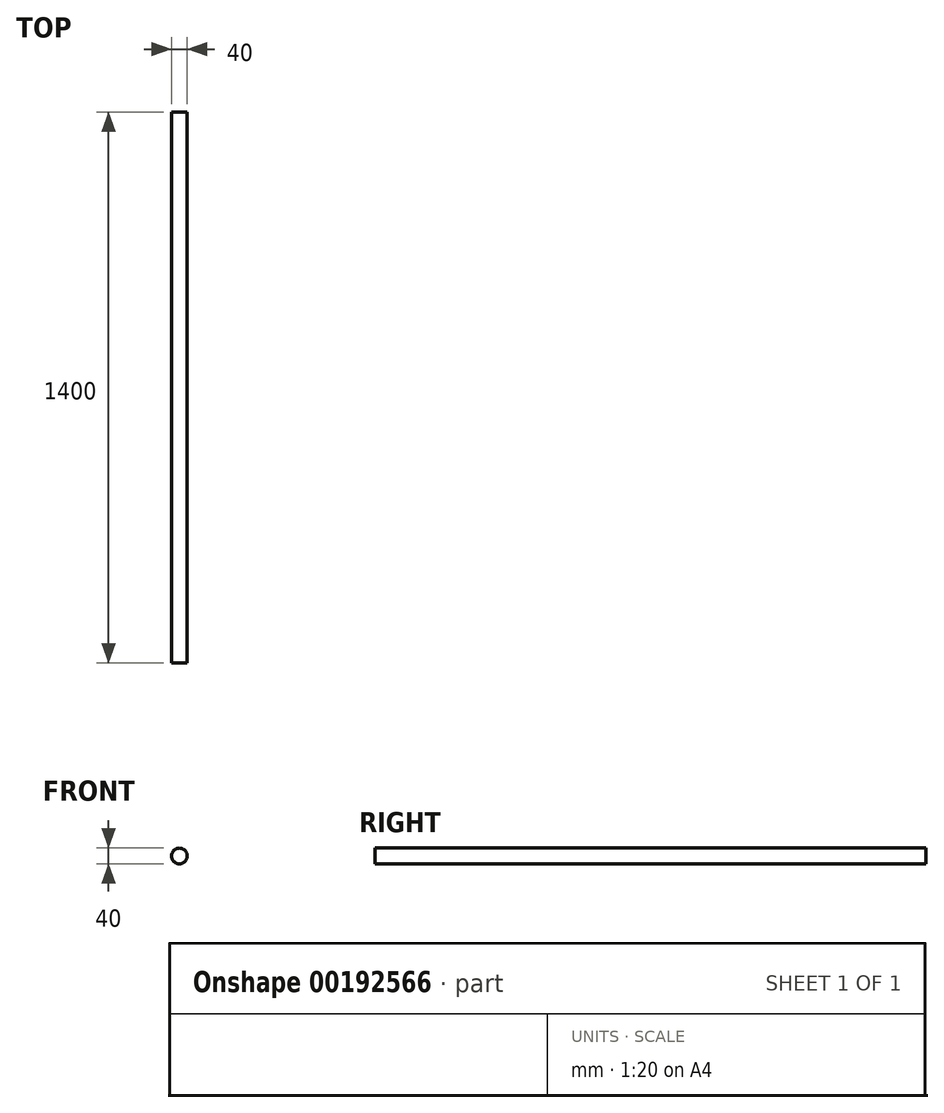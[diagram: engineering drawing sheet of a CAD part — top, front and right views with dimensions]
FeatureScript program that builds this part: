
annotation { "Feature Type Name" : "Feature", "Feature Type Description" : "" }
export const myFeature = defineFeature(function(context is Context, id is Id, definition is map)
    precondition{}
    {
        {
            var Q0;
            Q0=qCreatedBy(makeId("Front.planeOp"),FACE);
            var sketch = newSketch(context, id + "F0", { "sketchPlane" : qUnion([Q0])});
            skCircle(sketch, "E0", {"center": v(125, 0) * mm, "radius": 20 * mm});
            skLineSegment(sketch, "E1", {"start": v(0, 64.66) * mm, "end": v(0, -40.42) * mm, "construction": true});
            skCircle(sketch, "E2.MirrorC", {"center": v(-125, 0) * mm, "radius": 20 * mm});
            skSolve(sketch);
        }
        {
            var Q0;
            Q0=makeQuery(id+"F0.imprint","IMPRINT",FACE,{"disambiguationData":[TD([[makeQuery(id+"F0.imprint","IMPRINT",EDGE,{"derivedFrom":sQuery(id+"F0.wireOp",EDGE,"E0")}),1.0]])]});
            var Q1;
            Q1=makeQuery(id+"F0.imprint","IMPRINT",FACE,{"disambiguationData":[TD([[makeQuery(id+"F0.imprint","IMPRINT",EDGE,{"derivedFrom":sQuery(id+"F0.wireOp",EDGE,"E2.MirrorC")}),-1.0]])]});
            extrude(context, id + "F2", {"entities" : qUnion([Q0, Q1]), "endBound" : BoundingType.SYMMETRIC, "depth" : 1400 * mm});
        }
    });
